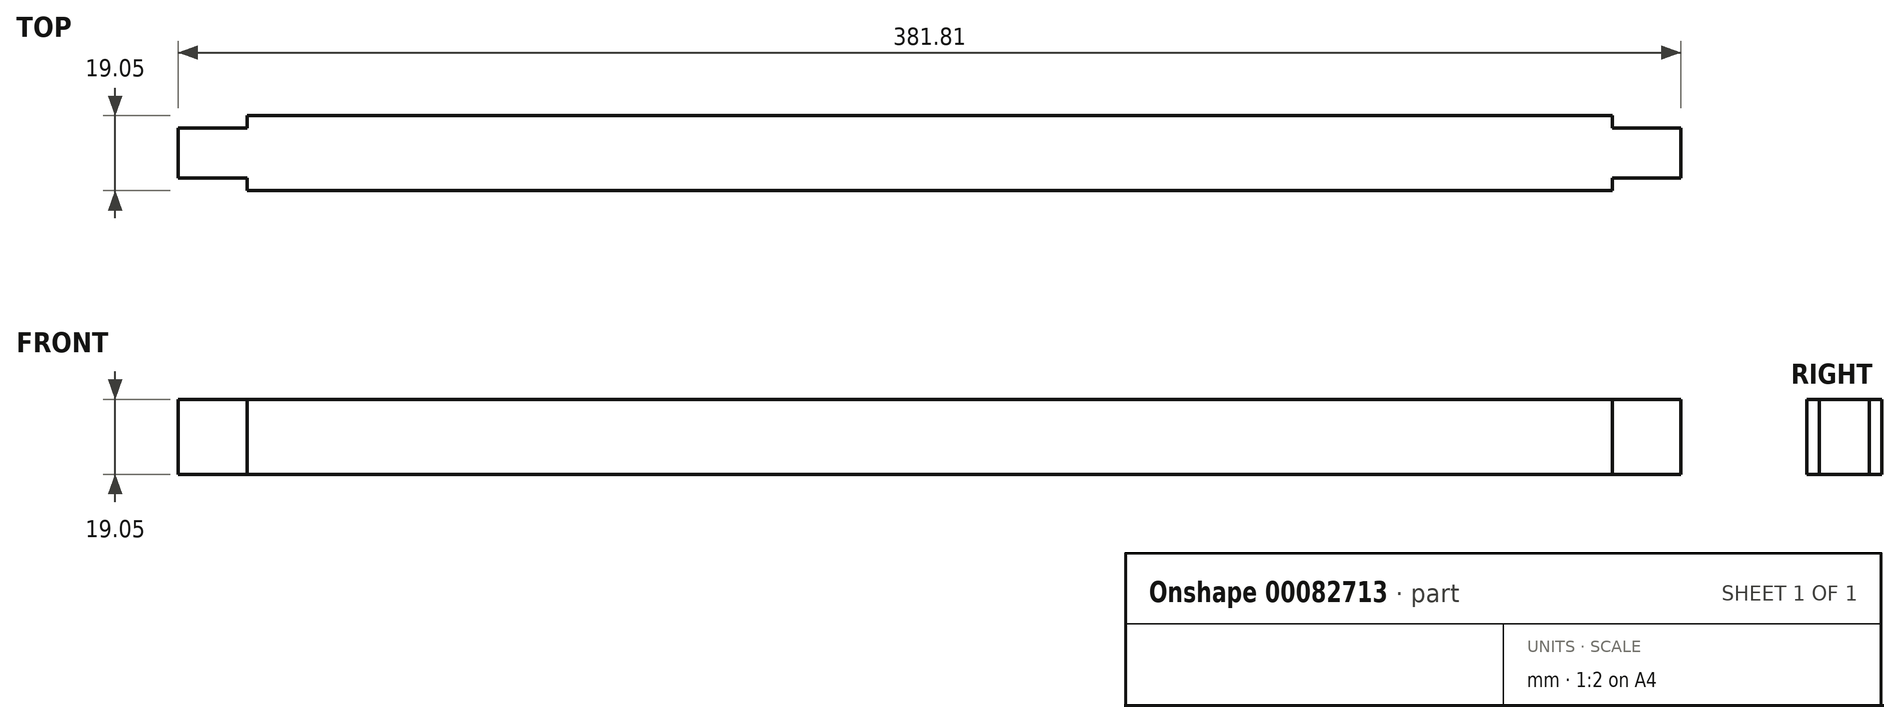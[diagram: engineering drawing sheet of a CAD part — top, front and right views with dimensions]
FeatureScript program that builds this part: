
annotation { "Feature Type Name" : "Feature", "Feature Type Description" : "" }
export const myFeature = defineFeature(function(context is Context, id is Id, definition is map)
    precondition{}
    {
        {
            var Q0;
            Q0=qCreatedBy(makeId("Top.planeOp"),FACE);
            var sketch = newSketch(context, id + "F0", { "sketchPlane" : qUnion([Q0])});
            skLineSegment(sketch, "E0.bottom", {"start": v(95.42, 4.53) * mm, "end": v(-251.47, 4.53) * mm});
            skLineSegment(sketch, "E0.left", {"start": v(95.42, 4.53) * mm, "end": v(95.42, 7.7) * mm});
            skLineSegment(sketch, "E0.right", {"start": v(-251.47, 4.53) * mm, "end": v(-251.47, 7.7) * mm});
            skLineSegment(sketch, "E1.bottom", {"start": v(-251.47, 7.7) * mm, "end": v(-268.93, 7.7) * mm});
            skLineSegment(sketch, "E1.right", {"start": v(-268.93, 7.7) * mm, "end": v(-268.93, 20.4) * mm});
            skLineSegment(sketch, "E2.bottom", {"start": v(112.88, 7.7) * mm, "end": v(95.42, 7.7) * mm});
            skLineSegment(sketch, "E2.left", {"start": v(112.88, 7.7) * mm, "end": v(112.88, 20.4) * mm});
            skLineSegment(sketch, "E3", {"start": v(-268.93, 14.06) * mm, "end": v(112.88, 14.06) * mm, "construction": true});
            skLineSegment(sketch, "E4.MirrorCS", {"start": v(112.88, 20.4) * mm, "end": v(95.42, 20.4) * mm});
            skLineSegment(sketch, "E5.MirrorCS", {"start": v(95.42, 23.58) * mm, "end": v(95.42, 20.4) * mm});
            skLineSegment(sketch, "E6.MirrorCS", {"start": v(95.42, 23.58) * mm, "end": v(-251.47, 23.58) * mm});
            skLineSegment(sketch, "E7.MirrorCS", {"start": v(-251.47, 23.58) * mm, "end": v(-251.47, 20.4) * mm});
            skLineSegment(sketch, "E8.MirrorCS", {"start": v(-251.47, 20.4) * mm, "end": v(-268.93, 20.4) * mm});
            skSolve(sketch);
        }
        {
            var Q0;
            Q0=qSketchRegion(id+"F0",true);
            extrude(context, id + "F1", {"entities" : qUnion([Q0]), "depth" : 19.05 * mm});
        }
    });
